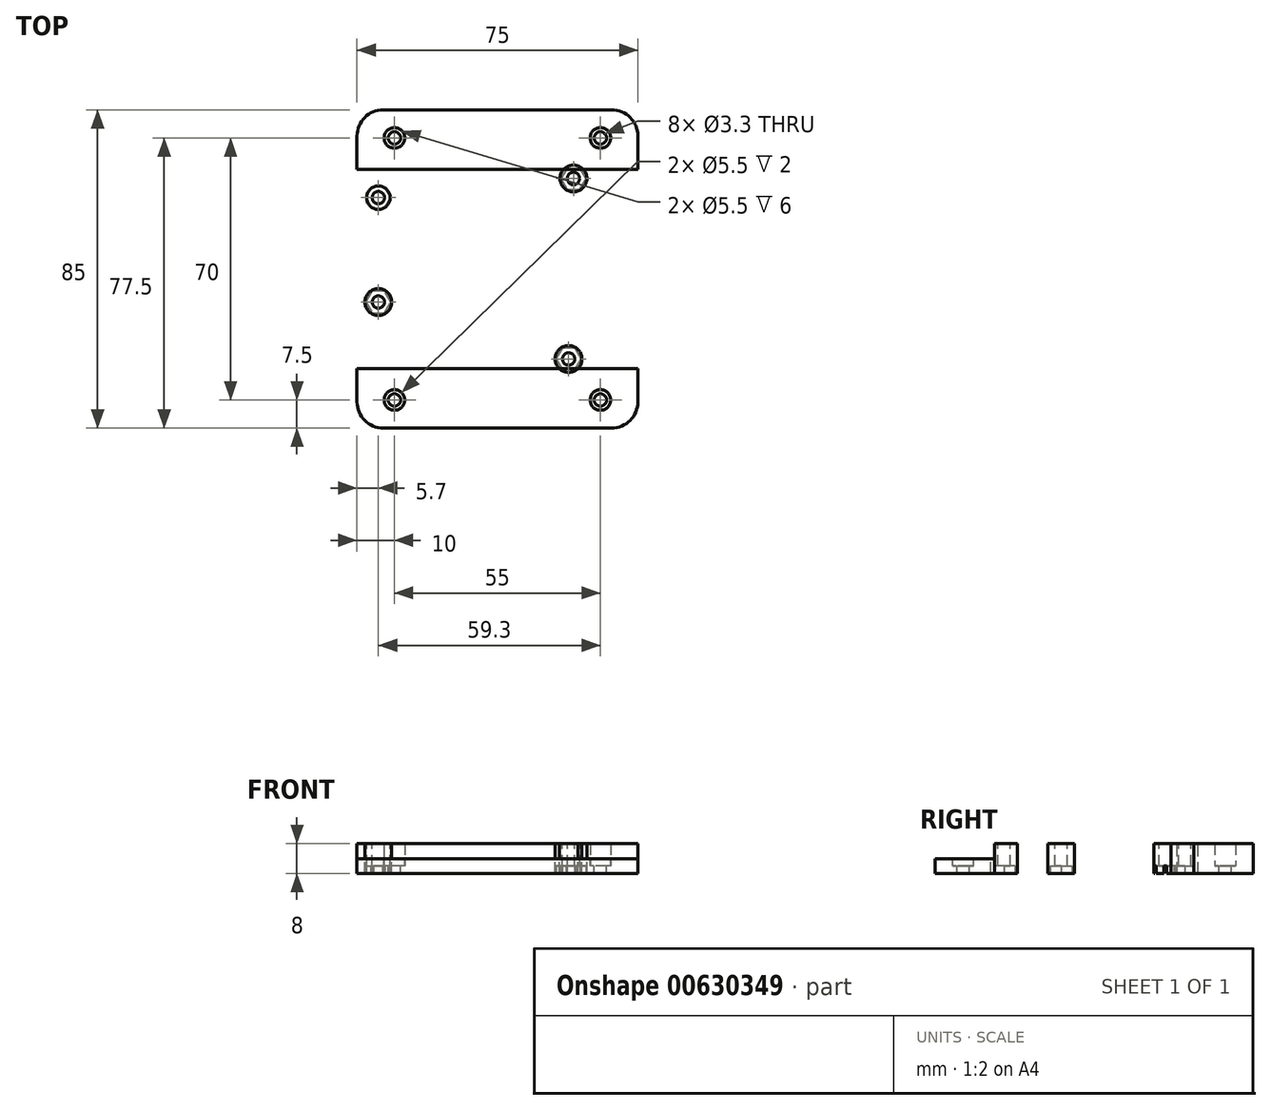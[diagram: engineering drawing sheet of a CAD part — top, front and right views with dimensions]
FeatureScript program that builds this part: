
annotation { "Feature Type Name" : "Feature", "Feature Type Description" : "" }
export const myFeature = defineFeature(function(context is Context, id is Id, definition is map)
    precondition{}
    {
        {
            var Q0;
            Q0=qCreatedBy(makeId("Top.planeOp"),FACE);
            var sketch = newSketch(context, id + "F0", { "sketchPlane" : qUnion([Q0])});
            skLineSegment(sketch, "E0.bottom", {"start": v(-37.5, 42.5) * mm, "end": v(37.5, 42.5) * mm});
            skLineSegment(sketch, "E0.top", {"start": v(-37.5, -42.5) * mm, "end": v(37.5, -42.5) * mm});
            skLineSegment(sketch, "E0.left", {"start": v(-37.5, 42.5) * mm, "end": v(-37.5, -42.5) * mm});
            skLineSegment(sketch, "E0.right", {"start": v(37.5, 42.5) * mm, "end": v(37.5, -42.5) * mm});
            skPoint(sketch, "E0.middle", {"position": v(0, 0) * mm});
            skCircle(sketch, "E1", {"center": v(-27.5, 35) * mm, "radius": 1.65 * mm});
            skCircle(sketch, "E2", {"center": v(27.5, 35) * mm, "radius": 1.65 * mm});
            skCircle(sketch, "E3", {"center": v(-27.5, -35) * mm, "radius": 1.65 * mm});
            skCircle(sketch, "E4", {"center": v(27.5, -35) * mm, "radius": 1.65 * mm});
            skCircle(sketch, "E5", {"center": v(-27.5, 35) * mm, "radius": 2.75 * mm});
            skCircle(sketch, "E6", {"center": v(27.5, 35) * mm, "radius": 2.75 * mm});
            skCircle(sketch, "E7", {"center": v(-27.5, -35) * mm, "radius": 2.75 * mm});
            skCircle(sketch, "E8", {"center": v(27.5, -35) * mm, "radius": 2.75 * mm});
            skLineSegment(sketch, "E9.bottom", {"start": v(-37.5, 26.65) * mm, "end": v(37.5, 26.65) * mm});
            skLineSegment(sketch, "E9.top", {"start": v(-37.5, -26.65) * mm, "end": v(37.5, -26.65) * mm});
            skLineSegment(sketch, "E9.left", {"start": v(-37.5, 26.65) * mm, "end": v(-37.5, -26.65) * mm});
            skLineSegment(sketch, "E9.right", {"start": v(37.5, 26.65) * mm, "end": v(37.5, -26.65) * mm});
            skCircle(sketch, "E10", {"center": v(20.3, 24.15) * mm, "radius": 1.65 * mm});
            skCircle(sketch, "E11", {"center": v(-31.8, 19.05) * mm, "radius": 1.65 * mm});
            skCircle(sketch, "E12", {"center": v(-31.8, -8.85) * mm, "radius": 1.65 * mm});
            skCircle(sketch, "E13", {"center": v(19, -24.05) * mm, "radius": 1.65 * mm});
            skLineSegment(sketch, "E14.bottom", {"start": v(-34.3, 26.65) * mm, "end": v(34.3, 26.65) * mm, "construction": true});
            skLineSegment(sketch, "E14.top", {"start": v(-34.3, -26.65) * mm, "end": v(34.3, -26.65) * mm});
            skLineSegment(sketch, "E14.left", {"start": v(-34.3, 26.65) * mm, "end": v(-34.3, -26.65) * mm, "construction": true});
            skLineSegment(sketch, "E14.right", {"start": v(34.3, 26.65) * mm, "end": v(34.3, -26.65) * mm, "construction": true});
            skCircle(sketch, "E15", {"center": v(-31.8, 19.05) * mm, "radius": 3.15 * mm});
            skCircle(sketch, "E16", {"center": v(-31.8, -8.85) * mm, "radius": 3.58 * mm});
            skCircle(sketch, "E17", {"center": v(20.3, 24.15) * mm, "radius": 3.58 * mm});
            skCircle(sketch, "E18", {"center": v(19, -24.05) * mm, "radius": 3.58 * mm});
            skSolve(sketch);
        }
        {
            var Q0;
            {var subQ1=sQuery(id+"F0.wireOp",EDGE,"E0.bottom");Q0=makeQuery(id+"F0.imprint","IMPRINT",FACE,{"disambiguationData":[TD([[makeQuery(id+"F0.imprint","IMPRINT",EDGE,{"derivedFrom":subQ1}),-1.0]])]});}
            var Q1;
            Q1=makeQuery(id+"F0.imprint","IMPRINT",FACE,{"disambiguationData":[TD([[makeQuery(id+"F0.imprint","IMPRINT",EDGE,{"derivedFrom":sQuery(id+"F0.wireOp",EDGE,"E1")}),-1.0]])]});
            var Q2;
            Q2=makeQuery(id+"F0.imprint","IMPRINT",FACE,{"disambiguationData":[TD([[makeQuery(id+"F0.imprint","IMPRINT",EDGE,{"derivedFrom":sQuery(id+"F0.wireOp",EDGE,"E2")}),-1.0]])]});
            var Q3;
            Q3=makeQuery(id+"F0.imprint","IMPRINT",FACE,{"disambiguationData":[TD([[makeQuery(id+"F0.imprint","IMPRINT",EDGE,{"derivedFrom":sQuery(id+"F0.wireOp",EDGE,"E10")}),-1.0]])]});
            var Q4;
            {var subQ0=sQuery(id+"F0.wireOp",EDGE,"E9.right");Q4=makeQuery(id+"F0.imprint","IMPRINT",FACE,{"disambiguationData":[TD([[makeQuery(id+"F0.imprint","IMPRINT",EDGE,{"derivedFrom":subQ0}),-1.0]])]});}
            var Q5;
            {var subQ0=sQuery(id+"F0.wireOp",EDGE,"E9.left");Q5=makeQuery(id+"F0.imprint","IMPRINT",FACE,{"disambiguationData":[TD([[makeQuery(id+"F0.imprint","IMPRINT",EDGE,{"derivedFrom":subQ0}),1.0]])]});}
            var Q6;
            {var subQ0=sQuery(id+"F0.wireOp",EDGE,"E0.top");Q6=makeQuery(id+"F0.imprint","IMPRINT",FACE,{"disambiguationData":[TD([[makeQuery(id+"F0.imprint","IMPRINT",EDGE,{"derivedFrom":subQ0}),1.0]])]});}
            var Q7;
            Q7=makeQuery(id+"F0.imprint","IMPRINT",FACE,{"disambiguationData":[TD([[makeQuery(id+"F0.imprint","IMPRINT",EDGE,{"derivedFrom":sQuery(id+"F0.wireOp",EDGE,"E3")}),-1.0]])]});
            var Q8;
            Q8=makeQuery(id+"F0.imprint","IMPRINT",FACE,{"disambiguationData":[TD([[makeQuery(id+"F0.imprint","IMPRINT",EDGE,{"derivedFrom":sQuery(id+"F0.wireOp",EDGE,"E4")}),-1.0]])]});
            var Q9;
            {var subQ0=sQuery(id+"F0.wireOp",EDGE,"E15");var subQ1=sQuery(id+"F0.wireOp",EDGE,"E14.left");var subQ2=makeQuery(id+"F0.imprint","INTERSECT",VERTEX,{"disambiguationData":[OD(0.0)],"derivedFrom":[subQ1,subQ0]});Q9=makeQuery(id+"F0.imprint","IMPRINT",FACE,{"disambiguationData":[TD([[makeQuery(id+"F0.imprint","IMPRINT",EDGE,{"disambiguationData":[TD([[subQ2,-1.0]])],"derivedFrom":subQ1}),-1.0]])]});}
            var Q10;
            Q10=makeQuery(id+"F0.imprint","IMPRINT",FACE,{"disambiguationData":[TD([[makeQuery(id+"F0.imprint","IMPRINT",EDGE,{"derivedFrom":sQuery(id+"F0.wireOp",EDGE,"E11")}),-1.0]])]});
            var Q11;
            {var subQ13=sQuery(id+"F0.wireOp",EDGE,"E14.right");Q11=makeQuery(id+"F0.imprint","IMPRINT",FACE,{"disambiguationData":[TD([[makeQuery(id+"F0.imprint","IMPRINT",EDGE,{"derivedFrom":subQ13}),-1.0]])]});}
            var Q12;
            Q12=makeQuery(id+"F0.imprint","IMPRINT",FACE,{"disambiguationData":[TD([[makeQuery(id+"F0.imprint","IMPRINT",EDGE,{"derivedFrom":sQuery(id+"F0.wireOp",EDGE,"E12")}),-1.0]])]});
            var Q13;
            {var subQ0=sQuery(id+"F0.wireOp",EDGE,"E16");var subQ1=sQuery(id+"F0.wireOp",EDGE,"E14.left");var subQ2=makeQuery(id+"F0.imprint","INTERSECT",VERTEX,{"disambiguationData":[OD(0.0)],"derivedFrom":[subQ1,subQ0]});Q13=makeQuery(id+"F0.imprint","IMPRINT",FACE,{"disambiguationData":[TD([[makeQuery(id+"F0.imprint","IMPRINT",EDGE,{"disambiguationData":[TD([[subQ2,-1.0]])],"derivedFrom":subQ1}),-1.0]])]});}
            var Q14;
            Q14=makeQuery(id+"F0.imprint","IMPRINT",FACE,{"disambiguationData":[TD([[makeQuery(id+"F0.imprint","IMPRINT",EDGE,{"derivedFrom":sQuery(id+"F0.wireOp",EDGE,"E13")}),-1.0]])]});
            var Q15;
            {var subQ0=sQuery(id+"F0.wireOp",EDGE,"E18");var subQ1=sQuery(id+"F0.wireOp",EDGE,"E14.top");var subQ2=makeQuery(id+"F0.imprint","INTERSECT",VERTEX,{"disambiguationData":[OD(0.0)],"derivedFrom":[subQ1,subQ0]});Q15=makeQuery(id+"F0.imprint","IMPRINT",FACE,{"disambiguationData":[TD([[makeQuery(id+"F0.imprint","IMPRINT",EDGE,{"disambiguationData":[TD([[subQ2,-1.0]])],"derivedFrom":subQ1}),-1.0]])]});}
            var Q16;
            {var subQ0=sQuery(id+"F0.wireOp",EDGE,"E17");var subQ1=sQuery(id+"F0.wireOp",EDGE,"E14.bottom");var subQ2=makeQuery(id+"F0.imprint","INTERSECT",VERTEX,{"disambiguationData":[OD(0.0)],"derivedFrom":[subQ1,subQ0]});Q16=makeQuery(id+"F0.imprint","IMPRINT",FACE,{"disambiguationData":[TD([[makeQuery(id+"F0.imprint","IMPRINT",EDGE,{"disambiguationData":[TD([[subQ2,-1.0]])],"derivedFrom":subQ1}),1.0]])]});}
            var Q17;
            {var subQ0=sQuery(id+"F0.wireOp",EDGE,"E17");var subQ1=sQuery(id+"F0.wireOp",EDGE,"E9.bottom");var subQ2=makeQuery(id+"F0.imprint","INTERSECT",VERTEX,{"disambiguationData":[OD(0.0)],"derivedFrom":[subQ1,subQ0]});Q17=makeQuery(id+"F0.imprint","IMPRINT",FACE,{"disambiguationData":[TD([[makeQuery(id+"F0.imprint","IMPRINT",EDGE,{"disambiguationData":[TD([[subQ2,-1.0]])],"derivedFrom":subQ1}),1.0]])]});}
            extrude(context, id + "F1", {"entities" : qUnion([Q0, Q1, Q2, Q3, Q4, Q5, Q6, Q7, Q8, Q9, Q10, Q11, Q12, Q13, Q14, Q15, Q16, Q17]), "oppositeDirection" : true, "depth" : 4 * mm, "offsetDistance" : 25 * mm});
        }
        {
            var Q0;
            Q0=makeQuery(id+"F0.imprint","IMPRINT",FACE,{"disambiguationData":[TD([[makeQuery(id+"F0.imprint","IMPRINT",EDGE,{"derivedFrom":sQuery(id+"F0.wireOp",EDGE,"E11")}),-1.0]])]});
            var Q1;
            Q1=makeQuery(id+"F0.imprint","IMPRINT",FACE,{"disambiguationData":[TD([[makeQuery(id+"F0.imprint","IMPRINT",EDGE,{"derivedFrom":sQuery(id+"F0.wireOp",EDGE,"E12")}),-1.0]])]});
            var Q2;
            Q2=makeQuery(id+"F0.imprint","IMPRINT",FACE,{"disambiguationData":[TD([[makeQuery(id+"F0.imprint","IMPRINT",EDGE,{"derivedFrom":sQuery(id+"F0.wireOp",EDGE,"E10")}),-1.0]])]});
            var Q3;
            {var subQ0=sQuery(id+"F0.wireOp",EDGE,"E17");var subQ1=sQuery(id+"F0.wireOp",EDGE,"E9.bottom");var subQ2=makeQuery(id+"F0.imprint","INTERSECT",VERTEX,{"disambiguationData":[OD(0.0)],"derivedFrom":[subQ1,subQ0]});Q3=makeQuery(id+"F0.imprint","IMPRINT",FACE,{"disambiguationData":[TD([[makeQuery(id+"F0.imprint","IMPRINT",EDGE,{"disambiguationData":[TD([[subQ2,-1.0]])],"derivedFrom":subQ1}),1.0]])]});}
            var Q4;
            Q4=makeQuery(id+"F0.imprint","IMPRINT",FACE,{"disambiguationData":[TD([[makeQuery(id+"F0.imprint","IMPRINT",EDGE,{"derivedFrom":sQuery(id+"F0.wireOp",EDGE,"E13")}),-1.0]])]});
            var Q5;
            {var subQ0=sQuery(id+"F0.wireOp",EDGE,"E18");var subQ1=sQuery(id+"F0.wireOp",EDGE,"E14.top");var subQ2=makeQuery(id+"F0.imprint","INTERSECT",VERTEX,{"disambiguationData":[OD(0.0)],"derivedFrom":[subQ1,subQ0]});Q5=makeQuery(id+"F0.imprint","IMPRINT",FACE,{"disambiguationData":[TD([[makeQuery(id+"F0.imprint","IMPRINT",EDGE,{"disambiguationData":[TD([[subQ2,-1.0]])],"derivedFrom":subQ1}),-1.0]])]});}
            extrude(context, id + "F2", {"entities" : qUnion([Q0, Q1, Q2, Q3, Q4, Q5]), "operationType" : NewBodyOperationType.ADD, "depth" : 4 * mm, "offsetDistance" : 25 * mm});
        }
        {
            var Q0;
            Q0=makeQuery(id+"F0.imprint","IMPRINT",FACE,{"disambiguationData":[TD([[makeQuery(id+"F0.imprint","IMPRINT",EDGE,{"derivedFrom":sQuery(id+"F0.wireOp",EDGE,"E1")}),-1.0]])]});
            var Q1;
            Q1=makeQuery(id+"F0.imprint","IMPRINT",FACE,{"disambiguationData":[TD([[makeQuery(id+"F0.imprint","IMPRINT",EDGE,{"derivedFrom":sQuery(id+"F0.wireOp",EDGE,"E2")}),-1.0]])]});
            var Q2;
            Q2=makeQuery(id+"F0.imprint","IMPRINT",FACE,{"disambiguationData":[TD([[makeQuery(id+"F0.imprint","IMPRINT",EDGE,{"derivedFrom":sQuery(id+"F0.wireOp",EDGE,"E3")}),-1.0]])]});
            var Q3;
            Q3=makeQuery(id+"F0.imprint","IMPRINT",FACE,{"disambiguationData":[TD([[makeQuery(id+"F0.imprint","IMPRINT",EDGE,{"derivedFrom":sQuery(id+"F0.wireOp",EDGE,"E4")}),-1.0]])]});
            extrude(context, id + "F3", {"entities" : qUnion([Q0, Q1, Q2, Q3]), "operationType" : NewBodyOperationType.REMOVE, "oppositeDirection" : true, "depth" : 2 * mm, "offsetDistance" : 25 * mm});
        }
        {
            var Q0;
            Q0=makeQuery(id+"F1.opExtrude","CAP_FACE",FACE,{"disambiguationData":[OSD([sQuery(id+"F0.wireOp",EDGE,"E0.bottom"),sQuery(id+"F0.wireOp",EDGE,"E0.top"),sQuery(id+"F0.wireOp",EDGE,"E0.left"),sQuery(id+"F0.wireOp",EDGE,"E0.right"),sQuery(id+"F0.wireOp",EDGE,"E1"),sQuery(id+"F0.wireOp",EDGE,"E2"),sQuery(id+"F0.wireOp",EDGE,"E3"),sQuery(id+"F0.wireOp",EDGE,"E4"),sQuery(id+"F0.wireOp",EDGE,"E9.left"),sQuery(id+"F0.wireOp",EDGE,"E9.right"),sQuery(id+"F0.wireOp",EDGE,"E10"),sQuery(id+"F0.wireOp",EDGE,"E11"),sQuery(id+"F0.wireOp",EDGE,"E12"),sQuery(id+"F0.wireOp",EDGE,"E13")])],"isStart":false});
            var sketch = newSketch(context, id + "F4", { "sketchPlane" : qUnion([Q0])});
            skCircle(sketch, "E19.cCircle", {"center": v(20.3, -24.15) * mm, "radius": 2.9 * mm, "construction": true});
            skLineSegment(sketch, "E19.0", {"start": v(21.97, -27.05) * mm, "end": v(18.63, -27.05) * mm});
            skLineSegment(sketch, "E19.1", {"start": v(18.63, -27.05) * mm, "end": v(16.95, -24.15) * mm});
            skLineSegment(sketch, "E19.2", {"start": v(16.95, -24.15) * mm, "end": v(18.63, -21.25) * mm});
            skLineSegment(sketch, "E19.3", {"start": v(18.63, -21.25) * mm, "end": v(21.97, -21.25) * mm});
            skLineSegment(sketch, "E19.4", {"start": v(21.97, -21.25) * mm, "end": v(23.65, -24.15) * mm});
            skLineSegment(sketch, "E19.5", {"start": v(23.65, -24.15) * mm, "end": v(21.97, -27.05) * mm});
            skPoint(sketch, "E19.0.midPoint", {"position": v(20.3, -27.05) * mm});
            skCircle(sketch, "E20.cCircle", {"center": v(-31.8, -19.05) * mm, "radius": 2.9 * mm, "construction": true});
            skLineSegment(sketch, "E20.0", {"start": v(-30.13, -21.95) * mm, "end": v(-33.47, -21.95) * mm});
            skLineSegment(sketch, "E20.1", {"start": v(-33.47, -21.95) * mm, "end": v(-35.15, -19.05) * mm});
            skLineSegment(sketch, "E20.2", {"start": v(-35.15, -19.05) * mm, "end": v(-33.47, -16.15) * mm});
            skLineSegment(sketch, "E20.3", {"start": v(-33.47, -16.15) * mm, "end": v(-30.13, -16.15) * mm});
            skLineSegment(sketch, "E20.4", {"start": v(-30.13, -16.15) * mm, "end": v(-28.45, -19.05) * mm});
            skLineSegment(sketch, "E20.5", {"start": v(-28.45, -19.05) * mm, "end": v(-30.13, -21.95) * mm});
            skPoint(sketch, "E20.0.midPoint", {"position": v(-31.8, -21.95) * mm});
            skCircle(sketch, "E21.cCircle", {"center": v(-31.8, 8.85) * mm, "radius": 2.9 * mm, "construction": true});
            skLineSegment(sketch, "E21.0", {"start": v(-30.13, 5.95) * mm, "end": v(-33.47, 5.95) * mm});
            skLineSegment(sketch, "E21.1", {"start": v(-33.47, 5.95) * mm, "end": v(-35.15, 8.85) * mm});
            skLineSegment(sketch, "E21.2", {"start": v(-35.15, 8.85) * mm, "end": v(-33.47, 11.75) * mm});
            skLineSegment(sketch, "E21.3", {"start": v(-33.47, 11.75) * mm, "end": v(-30.13, 11.75) * mm});
            skLineSegment(sketch, "E21.4", {"start": v(-30.13, 11.75) * mm, "end": v(-28.45, 8.85) * mm});
            skLineSegment(sketch, "E21.5", {"start": v(-28.45, 8.85) * mm, "end": v(-30.13, 5.95) * mm});
            skPoint(sketch, "E21.0.midPoint", {"position": v(-31.8, 5.95) * mm});
            skCircle(sketch, "E22.cCircle", {"center": v(19, 24.05) * mm, "radius": 2.9 * mm, "construction": true});
            skLineSegment(sketch, "E22.0", {"start": v(20.67, 21.15) * mm, "end": v(17.33, 21.15) * mm});
            skLineSegment(sketch, "E22.1", {"start": v(17.33, 21.15) * mm, "end": v(15.65, 24.05) * mm});
            skLineSegment(sketch, "E22.2", {"start": v(15.65, 24.05) * mm, "end": v(17.33, 26.95) * mm});
            skLineSegment(sketch, "E22.3", {"start": v(17.33, 26.95) * mm, "end": v(20.67, 26.95) * mm});
            skLineSegment(sketch, "E22.4", {"start": v(20.67, 26.95) * mm, "end": v(22.35, 24.05) * mm});
            skLineSegment(sketch, "E22.5", {"start": v(22.35, 24.05) * mm, "end": v(20.67, 21.15) * mm});
            skPoint(sketch, "E22.0.midPoint", {"position": v(19, 21.15) * mm});
            skSolve(sketch);
        }
        {
            var Q0;
            Q0=makeQuery(id+"F4.imprint","IMPRINT",FACE,{"disambiguationData":[TD([[makeQuery(id+"F4.imprint","IMPRINT",EDGE,{"derivedFrom":sQuery(id+"F4.wireOp",EDGE,"E19.0")}),-1.0]])]});
            var Q1;
            Q1=makeQuery(id+"F4.imprint","IMPRINT",FACE,{"disambiguationData":[TD([[makeQuery(id+"F4.imprint","IMPRINT",EDGE,{"derivedFrom":sQuery(id+"F4.wireOp",EDGE,"E20.0")}),-1.0]])]});
            var Q2;
            Q2=makeQuery(id+"F4.imprint","IMPRINT",FACE,{"disambiguationData":[TD([[makeQuery(id+"F4.imprint","IMPRINT",EDGE,{"derivedFrom":sQuery(id+"F4.wireOp",EDGE,"E22.0")}),-1.0]])]});
            var Q3;
            Q3=makeQuery(id+"F4.imprint","IMPRINT",FACE,{"disambiguationData":[TD([[makeQuery(id+"F4.imprint","IMPRINT",EDGE,{"derivedFrom":sQuery(id+"F4.wireOp",EDGE,"E21.0")}),-1.0]])]});
            extrude(context, id + "F5", {"entities" : qUnion([Q0, Q1, Q2, Q3]), "operationType" : NewBodyOperationType.REMOVE, "oppositeDirection" : true, "depth" : 2 * mm, "offsetDistance" : 25 * mm});
        }
        {
            var Q0;
            Q0=makeQuery(id+"F1.opExtrude","SWEPT_EDGE",EDGE,{"disambiguationData":[OSD([sQuery(id+"F0.wireOp",EDGE,"E0.bottom"),sQuery(id+"F0.wireOp",EDGE,"E0.left")])]});
            var Q1;
            Q1=makeQuery(id+"F1.opExtrude","SWEPT_EDGE",EDGE,{"disambiguationData":[OSD([sQuery(id+"F0.wireOp",EDGE,"E0.top"),sQuery(id+"F0.wireOp",EDGE,"E0.left")])]});
            var Q2;
            Q2=makeQuery(id+"F1.opExtrude","SWEPT_EDGE",EDGE,{"disambiguationData":[OSD([sQuery(id+"F0.wireOp",EDGE,"E0.top"),sQuery(id+"F0.wireOp",EDGE,"E0.right")])]});
            var Q3;
            Q3=makeQuery(id+"F1.opExtrude","SWEPT_EDGE",EDGE,{"disambiguationData":[OSD([sQuery(id+"F0.wireOp",EDGE,"E0.bottom"),sQuery(id+"F0.wireOp",EDGE,"E0.right")])]});
            fillet(context, id + "F6", {"entities" : qUnion([Q0, Q1, Q2, Q3]), "radius" : 7 * mm, "tangentPropagation" : true, "allowEdgeOverflow" : false});
        }
    });
